FCSTD DOCUMENT  (FreeCAD 1.0R39319 (Git))
Label: Unnamed
License: All rights reserved
LicenseURL: https://en.wikipedia.org/wiki/All_rights_reserved
objects: Sketcher::SketchObject×1, PartDesign::Body×1, Spreadsheet::Sheet×1
note: 3 computed .brp shape members not serialized (recipe doc carries the construction recipe); baked Part::Feature solids carry a one-line shape summary decoded from their .brp

FEATURE [Sketcher::SketchObject] Sketch
  ArcFitTolerance = 1e-06
  AttachmentSupport = -> [XY_Plane]
  FullyConstrained = false
  MakeInternals = false
  MapMode = 5
  expr: Constraints[1] = <<Sheet1>>.x_center_max_dis
  expr: Constraints[39] = <<Sheet1>>.side_rad
  expr: Constraints[40] = <<Sheet1>>.side_rad
  expr: Constraints[46] = <<Sheet1>>.side_ria_dis
  expr: Constraints[47] = <<Sheet1>>.side_y_inner
  expr: Constraints[48] = <<Sheet1>>.side_y_outer
  expr: Constraints[49] = <<Sheet1>>.y_center_max
  expr: Constraints[50] = <<Sheet1>>.y_center_min
  expr: Constraints[51] = <<Sheet1>>.y_center_flange
  expr: Constraints[52] = <<Sheet1>>.y_centerbox_max
  expr: Constraints[53] = <<Sheet1>>.y_bottomfrom_min
  expr: Constraints[54] = <<Sheet1>>.bottomstep_y
  expr: Constraints[93] = <<Sheet1>>.x_center_max_dis
  expr: Constraints[94] = <<Sheet1>>.x_center_inner_dis
  expr: Constraints[95] = <<Sheet1>>.x_center_inside_dis
  expr: Constraints[96] = <<Sheet1>>.x_bottombox_max_dis
  expr: Constraints[98] = <<Sheet1>>.y_bottomfrom_min / 2
  sketch-geometry (48):
    g0: LineSegment StartX=-25 StartY=0 StartZ=0 EndX=25 EndY=0 EndZ=0
    g1: GeomPoint X=0 Y=0 Z=0
    g2: LineSegment StartX=-25 StartY=0 StartZ=0 EndX=-25 EndY=30 EndZ=0
    g3: LineSegment StartX=-25 StartY=30 StartZ=0 EndX=-16.25 EndY=30 EndZ=0
    g4: LineSegment StartX=-16.25 StartY=30 StartZ=0 EndX=-16.25 EndY=14 EndZ=0
    g5: LineSegment StartX=-16.25 StartY=14 StartZ=0 EndX=-19.04 EndY=14 EndZ=0
    g6: LineSegment StartX=0 StartY=22.6 StartZ=0 EndX=-5.46969 EndY=22.6 EndZ=0
    g7: LineSegment StartX=-5.46969 StartY=22.6 StartZ=0 EndX=-8.1 EndY=18.0152 EndZ=0
    g8: LineSegment StartX=-8.1 StartY=18.0152 StartZ=0 EndX=-8.1 EndY=9.5 EndZ=0
    g9: LineSegment StartX=-8.1 StartY=9.5 StartZ=0 EndX=-19.04 EndY=9.5 EndZ=0
    g10: LineSegment StartX=-19.04 StartY=14 StartZ=0 EndX=-19.04 EndY=9.5 EndZ=0
    g11: LineSegment StartX=-15.67 StartY=0 StartZ=0 EndX=-15.67 EndY=-14 EndZ=0
    g12: LineSegment StartX=-15.67 StartY=-14 StartZ=0 EndX=0 EndY=-14 EndZ=0
    g13: LineSegment StartX=-15.67 StartY=-14 StartZ=0 EndX=-14.0121 EndY=-16 EndZ=0
    g14: LineSegment StartX=-14.0121 StartY=-16 StartZ=0 EndX=0 EndY=-16 EndZ=0
    g15: ArcOfCircle CenterX=-27.5939 CenterY=21.9058 CenterZ=0 NormalX=0 NormalY=0 NormalZ=1 AngleXU=0 Radius=3 StartAngle=3.78168 EndAngle=5.75679
    g16: ArcOfCircle CenterX=-27.5939 CenterY=7.3178 CenterZ=0 NormalX=0 NormalY=0 NormalZ=1 AngleXU=0 Radius=3 StartAngle=0.526392 EndAngle=2.5015
    g17: LineSegment StartX=-30 StartY=25 StartZ=0 EndX=-30 EndY=5 EndZ=0
    g18: LineSegment StartX=-30 StartY=25 StartZ=0 EndX=-46.9388 EndY=23 EndZ=0
    g19: LineSegment StartX=-30 StartY=5 StartZ=0 EndX=-46.9388 EndY=7 EndZ=0
    g20: LineSegment StartX=-46.9388 StartY=23 StartZ=0 EndX=-46.9388 EndY=7 EndZ=0
    g21: GeomPoint X=-30 Y=15 Z=0
    g22: GeomPoint X=-25 Y=15 Z=0
    g23: GeomPoint X=-46.9388 Y=15 Z=0
    g24: LineSegment [constr] StartX=-30 StartY=15 StartZ=0 EndX=-25 EndY=15 EndZ=0
    g25: LineSegment StartX=25 StartY=0 StartZ=0 EndX=25 EndY=30 EndZ=0
    g26: LineSegment StartX=25 StartY=30 StartZ=0 EndX=16.25 EndY=30 EndZ=0
    g27: LineSegment StartX=16.25 StartY=30 StartZ=0 EndX=16.25 EndY=14 EndZ=0
    g28: LineSegment StartX=16.25 StartY=14 StartZ=0 EndX=19.04 EndY=14 EndZ=0
    g29: LineSegment StartX=0 StartY=22.6 StartZ=0 EndX=5.46969 EndY=22.6 EndZ=0
    g30: LineSegment StartX=5.46969 StartY=22.6 StartZ=0 EndX=8.1 EndY=18.0152 EndZ=0
    g31: LineSegment StartX=8.1 StartY=18.0152 StartZ=0 EndX=8.1 EndY=9.5 EndZ=0
    g32: LineSegment StartX=8.1 StartY=9.5 StartZ=0 EndX=19.04 EndY=9.5 EndZ=0
    g33: LineSegment StartX=19.04 StartY=14 StartZ=0 EndX=19.04 EndY=9.5 EndZ=0
    g34: LineSegment StartX=14.33 StartY=0 StartZ=0 EndX=14.33 EndY=-14 EndZ=0
    g35: LineSegment StartX=14.33 StartY=-14 StartZ=0 EndX=0 EndY=-14 EndZ=0
    g36: LineSegment StartX=14.33 StartY=-14 StartZ=0 EndX=12.6721 EndY=-16 EndZ=0
    g37: LineSegment StartX=12.6721 StartY=-16 StartZ=0 EndX=0 EndY=-16 EndZ=0
    g38: ArcOfCircle CenterX=27.5939 CenterY=21.9058 CenterZ=0 NormalX=0 NormalY=0 NormalZ=1 AngleXU=0 Radius=3 StartAngle=3.66798 EndAngle=5.64309
    g39: ArcOfCircle CenterX=27.5939 CenterY=7.3178 CenterZ=0 NormalX=0 NormalY=0 NormalZ=1 AngleXU=0 Radius=3 StartAngle=0.640091 EndAngle=2.6152
    g40: LineSegment StartX=30.0972 StartY=24.9607 StartZ=0 EndX=47.0405 EndY=22.999 EndZ=0
    g41: LineSegment StartX=30.1001 StartY=5.01158 StartZ=0 EndX=47.0405 EndY=6.99898 EndZ=0
    g42: LineSegment StartX=47.0405 StartY=22.999 StartZ=0 EndX=47.0405 EndY=6.99898 EndZ=0
    g43: GeomPoint X=30 Y=15 Z=0
    g44: GeomPoint X=47.0405 Y=14.999 Z=0
    g45: LineSegment [constr] StartX=30 StartY=15 StartZ=0 EndX=25 EndY=15 EndZ=0
    g46: LineSegment StartX=30 StartY=25 StartZ=0 EndX=30 EndY=5 EndZ=0
    g47: Circle CenterX=0 CenterY=-9 CenterZ=0 NormalX=0 NormalY=0 NormalZ=1 AngleXU=0 Radius=2.91456
  constraints (118):
    c: PointOnObject(g0,g-1)
    c: DistanceX(g0,g0) = 50
    c: Symmetric(g0,g0,g1)
    c: Coincident(g1,g-1)
    c: Coincident(g2,g0)
    c: Vertical(g2)
    c: Coincident(g3,g2)
    c: Horizontal(g3)
    c: Coincident(g4,g3)
    c: Vertical(g4)
    c: Coincident(g5,g4)
    c: Horizontal(g5)
    c: PointOnObject(g6,g-2)
    c: Horizontal(g6)
    c: Coincident(g7,g6)
    c: Coincident(g8,g7)
    c: Vertical(g8)
    c: Coincident(g9,g8)
    c: Horizontal(g9)
    c: Coincident(g10,g5)
    c: Vertical(g10)
    c: Coincident(g9,g10)
    c: PointOnObject(g11,g0)
    c: Vertical(g11)
    c: Coincident(g12,g11)
    c: PointOnObject(g12,g-2)
    c: Horizontal(g12)
    c: Coincident(g13,g11)
    c: Coincident(g14,g13)
    c: PointOnObject(g14,g-2)
    c: Horizontal(g14)
    c: PointOnObject(g16,g2)
    c: Vertical(g17)
    c: PointOnObject(g16,g17)
    c: Coincident(g18,g17)
    c: Coincident(g19,g17)
    c: Coincident(g20,g18)
    c: Coincident(g20,g19)
    c: Vertical(g20)
    c: Radius(g15) = 3
    c: Radius(g16) = 3
    c: Symmetric(g17,g17,g21)
    c: Symmetric(g2,g2,g22)
    c: Horizontal(g22,g21)
    c: Symmetric(g20,g20,g23)
    c: Horizontal(g23,g21)
    c: Distance(g17,g2) = 5
    c: DistanceY(g17,g17) = 20
    c: DistanceY(g20,g20) = 16
    c: DistanceY(g2,g2) = 30
    c: Distance(g0,g9) = 9.5
    c: DistanceY(g4,g4) = 16
    c: Distance(g0,g6) = 22.6
    c: Distance(g12,g0) = 14
    c: Distance(g14,g12) = 2
    c: PointOnObject(g15,g17)
    c: PointOnObject(g15,g2)
    c: Vertical(g15,g16)
    c: Coincident(g24,g21)
    c: Coincident(g24,g22)
    c: Vertical(g25)
    c: Coincident(g26,g25)
    c: Horizontal(g26)
    c: Coincident(g27,g26)
    c: Vertical(g27)
    c: Coincident(g28,g27)
    c: Horizontal(g28)
    c: Horizontal(g29)
    c: Coincident(g30,g29)
    c: Coincident(g31,g30)
    c: Vertical(g31)
    c: Coincident(g32,g31)
    c: Horizontal(g32)
    c: Coincident(g33,g28)
    c: Vertical(g33)
    c: Coincident(g32,g33)
    c: Vertical(g34)
    c: Coincident(g35,g34)
    c: Horizontal(g35)
    c: Coincident(g36,g34)
    c: Coincident(g37,g36)
    c: Horizontal(g37)
    c: PointOnObject(g39,g25)
    c: Coincident(g42,g40)
    c: Coincident(g42,g41)
    c: Vertical(g42)
    c: Radius(g38) = 3
    c: Radius(g39) = 3
    c: Symmetric(g42,g42,g44)
    c: Distance(g37,g35) = 2
    c: PointOnObject(g38,g25)
    c: Coincident(g45,g43)
    c: Vertical(g46)
    c: Distance(g2,g25) = 50
    c: Distance(g27,g4) = 32.5
    c: Distance(g31,g8) = 16.2
    c: Distance(g34,g11) = 30
    c: PointOnObject(g47,g-2)
    c: Distance(g47,g14) = 7
    c: Coincident(g37,g14)
    c: PointOnObject(g35,g-2)
    c: PointOnObject(g34,g0)
    c: Distance(g-2,g11) = 15.67
    c: Equal(g32,g9)
    c: Equal(g10,g33)
    c: Equal(g5,g28)
    c: Equal(g4,g27)
    c: Equal(g29,g6)
    c: Equal(g30,g7)
    c: Equal(g31,g8)
    c: Coincident(g29,g6)
    c: Equal(g20,g42)
    c: Equal(g18,g40)
    c: Equal(g19,g41)
    c: Equal(g17,g46)
    c: Equal(g13,g36)
    c: PointOnObject(g25,g0)
    c: Equal(g2,g25)
FEATURE [PartDesign::Body] Body
  AllowCompound = false
  Group = -> [Sketch]
  Origin = -> Origin
FEATURE [Spreadsheet::Sheet] Spreadsheet  label="Sheet1"
  cells = A1='x_center_max_dis ; B1(x_center_max_dis)=50; A2='x_center_inner_dis; B2(x_center_inner_dis)=32.5; A3='x_center_inside_dis; B3(x_center_inside_dis)=16.2; A4='x_centerbox_dis; B4(x_centerbox_dis)=6.3; A5='x_bottombox_max_dis; B5(x_bottombox_max_dis)=30; A6='bottom_circle_dia; B6(bottom_circle_dia)=8; A7='y_center_max; B7(y_center_max)=30; A8='y_center_min; B8(y_center_min)=9.5; A9='y_center_frommintomax; B9(y_center_frommintomax)=20.5; A10='y_center_flange; B10(y_center_flange)=16; A11='y_centerbox_max; B11(y_centerbox_max)=22.6; A12='side_rad; B12(side_rad)=3; A13='side_y_inner; B13(side_y_inner)=20; A14='side_y_outer; B14(side_y_outer)=16; A15='side_ria_dis; B15(side_ria_dis)=5; A16='y_bottomfrom_min; B16(y_bottomfrom_min)=14; A17='bottomstep_y ; B17(bottomstep_y)=2; A18='bottomsetp_x; B18(bottomsetp_x)==B5 - 4; A19='bottomcut_x; B19(bottomcut_x)=4
